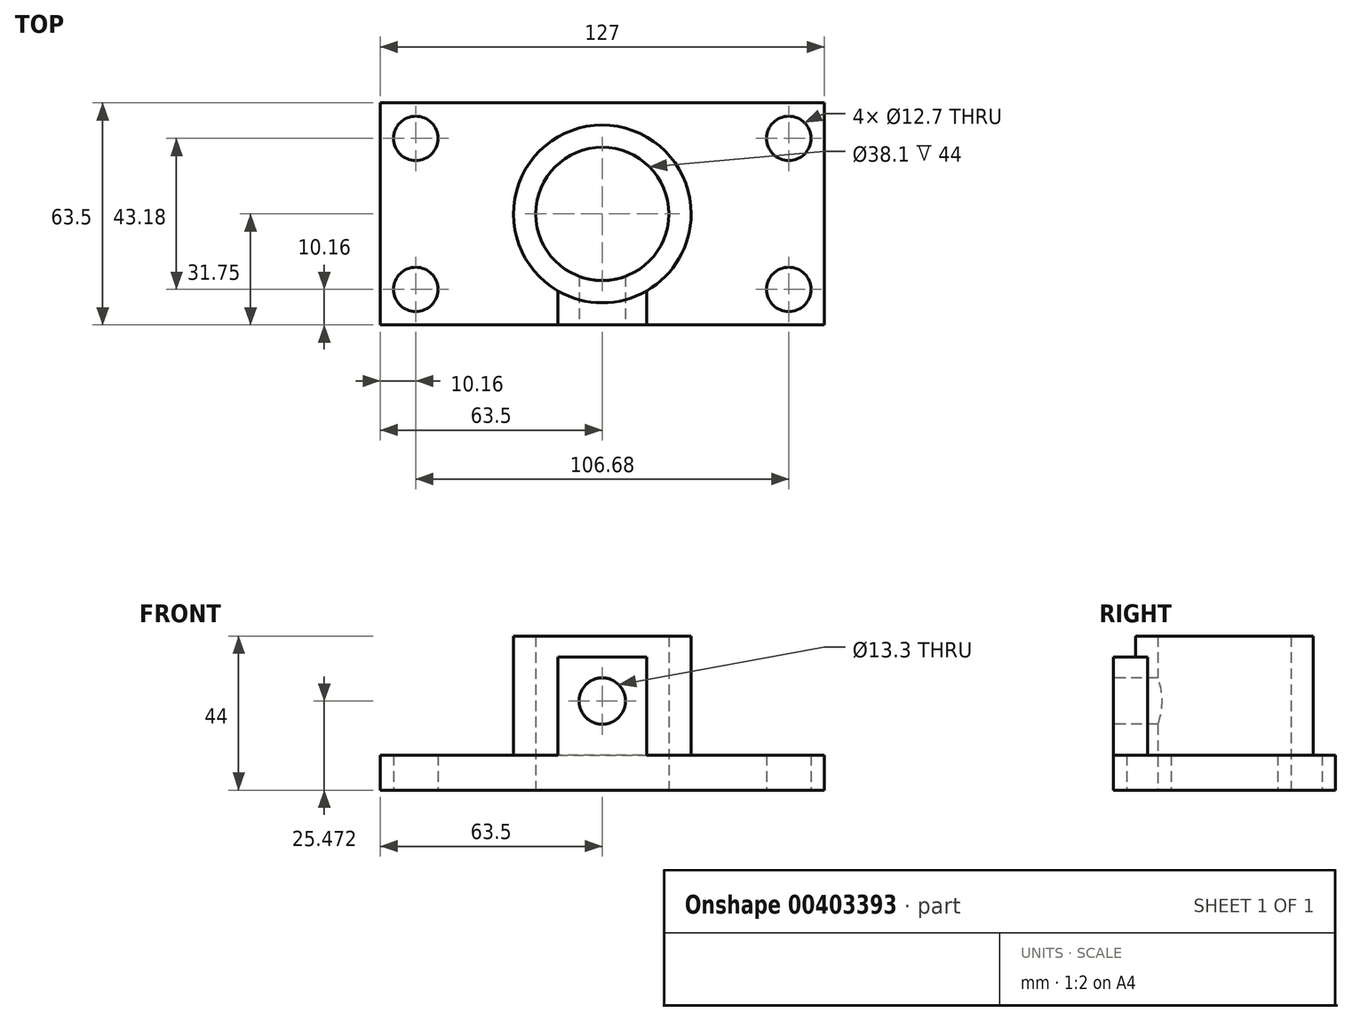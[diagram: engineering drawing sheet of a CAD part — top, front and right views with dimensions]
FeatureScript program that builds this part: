
annotation { "Feature Type Name" : "Feature", "Feature Type Description" : "" }
export const myFeature = defineFeature(function(context is Context, id is Id, definition is map)
    precondition{}
    {
        {
            var Q0;
            Q0=qCreatedBy(makeId("Top.planeOp"),FACE);
            var sketch = newSketch(context, id + "F0", { "sketchPlane" : qUnion([Q0])});
            skLineSegment(sketch, "E0.bottom", {"start": v(-63.5, 31.75) * mm, "end": v(63.5, 31.75) * mm});
            skLineSegment(sketch, "E0.top", {"start": v(-63.5, -31.75) * mm, "end": v(63.5, -31.75) * mm});
            skLineSegment(sketch, "E0.left", {"start": v(-63.5, 31.75) * mm, "end": v(-63.5, -31.75) * mm});
            skLineSegment(sketch, "E0.right", {"start": v(63.5, 31.75) * mm, "end": v(63.5, -31.75) * mm});
            skCircle(sketch, "E1", {"center": v(-53.34, 21.59) * mm, "radius": 6.35 * mm});
            skCircle(sketch, "E2", {"center": v(53.34, 21.59) * mm, "radius": 6.35 * mm});
            skCircle(sketch, "E3", {"center": v(-53.34, -21.59) * mm, "radius": 6.35 * mm});
            skCircle(sketch, "E4", {"center": v(53.34, -21.59) * mm, "radius": 6.35 * mm});
            skCircle(sketch, "E5", {"center": v(0, 0) * mm, "radius": 25.4 * mm});
            skCircle(sketch, "E6", {"center": v(0, 0) * mm, "radius": 19.05 * mm});
            skLineSegment(sketch, "E7", {"start": v(-12.7, -22) * mm, "end": v(-12.7, -31.75) * mm});
            skLineSegment(sketch, "E8", {"start": v(12.7, -31.75) * mm, "end": v(12.7, -22) * mm});
            skSolve(sketch);
        }
        {
            var Q0;
            Q0=makeQuery(id+"F0.imprint","IMPRINT",FACE,{"disambiguationData":[TD([[makeQuery(id+"F0.imprint","IMPRINT",EDGE,{"derivedFrom":sQuery(id+"F0.wireOp",EDGE,"E0.bottom")}),-1.0]])]});
            extrude(context, id + "F1", {"entities" : qUnion([Q0]), "depth" : 10 * mm});
        }
        {
            var Q0;
            Q0=makeQuery(id+"F0.imprint","IMPRINT",FACE,{"disambiguationData":[TD([[makeQuery(id+"F0.imprint","IMPRINT",EDGE,{"derivedFrom":sQuery(id+"F0.wireOp",EDGE,"E6")}),-1.0]])]});
            extrude(context, id + "F2", {"entities" : qUnion([Q0]), "operationType" : NewBodyOperationType.ADD, "depth" : 44 * mm});
        }
        {
            var Q0;
            {var subQ0=sQuery(id+"F0.wireOp",EDGE,"E7");Q0=makeQuery(id+"F0.imprint","IMPRINT",FACE,{"disambiguationData":[TD([[makeQuery(id+"F0.imprint","IMPRINT",EDGE,{"derivedFrom":subQ0}),1.0]])]});}
            extrude(context, id + "F3", {"entities" : qUnion([Q0]), "operationType" : NewBodyOperationType.ADD, "depth" : 38 * mm});
        }
        {
            var Q0;
            {var subQ0=sQuery(id+"F0.wireOp",EDGE,"E0.top");Q0=makeQuery(id+"F3.boolean.opBoolean","MERGE",FACE,{"derivedFrom":[makeQuery(id+"F1.opExtrude","SWEPT_FACE",FACE,{"disambiguationData":[OSD([subQ0]),TDD([makeQuery(id+"F0.imprint","IMPRINT",EDGE,{"disambiguationData":[TD([[makeQuery(id+"F0.imprint","INTERSECT",VERTEX,{"derivedFrom":[subQ0,sQuery(id+"F0.wireOp",EDGE,"E0.left")]}),-1.0]])],"derivedFrom":subQ0})])]}),makeQuery(id+"F1.opExtrude","SWEPT_FACE",FACE,{"disambiguationData":[OSD([subQ0]),TDD([makeQuery(id+"F0.imprint","IMPRINT",EDGE,{"disambiguationData":[TD([[makeQuery(id+"F0.imprint","INTERSECT",VERTEX,{"derivedFrom":[subQ0,sQuery(id+"F0.wireOp",EDGE,"E0.right")]}),1.0]])],"derivedFrom":subQ0})])]}),makeQuery(id+"F3.opExtrude","SWEPT_FACE",FACE,{"disambiguationData":[OSD([subQ0])]})]});}
            var sketch = newSketch(context, id + "F4", { "sketchPlane" : qUnion([Q0])});
            skCircle(sketch, "E9", {"center": v(0, 25.47) * mm, "radius": 6.65 * mm});
            skSolve(sketch);
        }
        {
            var Q0;
            Q0=makeQuery(id+"F4.imprint","IMPRINT",FACE,{"disambiguationData":[TD([[makeQuery(id+"F4.imprint","IMPRINT",EDGE,{"derivedFrom":sQuery(id+"F4.wireOp",EDGE,"E9")}),1.0]])]});
            var Q1;
            Q1=makeQuery(id+"F2.opExtrude","SWEPT_FACE",FACE,{"disambiguationData":[OSD([sQuery(id+"F0.wireOp",EDGE,"E6")])]});
            extrude(context, id + "F5", {"entities" : qUnion([Q0]), "operationType" : NewBodyOperationType.REMOVE, "endBound" : BoundingType.UP_TO_SURFACE, "oppositeDirection" : true, "endBoundEntityFace" : qUnion([Q1]), "depth" : 25.4 * mm});
        }
    });
